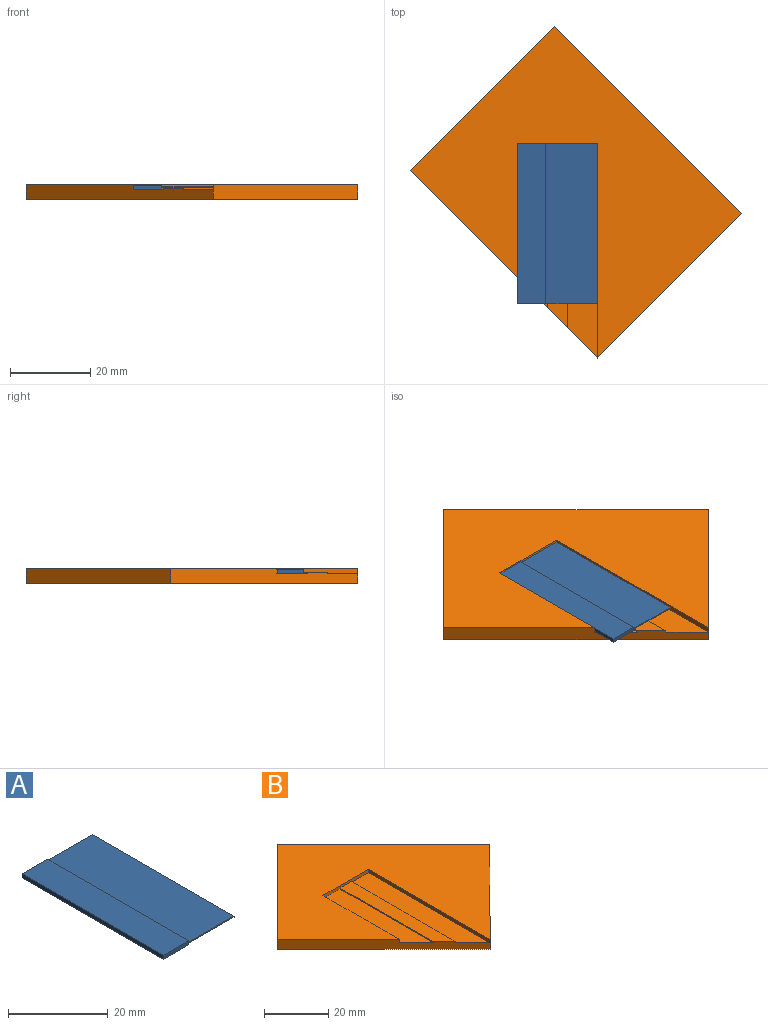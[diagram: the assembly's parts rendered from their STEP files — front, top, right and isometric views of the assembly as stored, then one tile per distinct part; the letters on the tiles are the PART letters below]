
ASSEMBLY  parts=2 mates=1
PART A: 10 faces, bbox 20x40x1 mm
  f0: plane 40x0.38mm, normal (1,0,0), area 15mm2, adj f2,f4,f6,f9
  f1: plane 40x1mm, normal (-1,0,0), area 40mm2, adj f2,f4,f5,f6
  f2: plane 20x1mm, normal (0,-1,0), area 10.4mm2, adj f0,f1,f3,f5,f6,f7,f8,f9
  f3: plane 40x0.38mm, normal (1,0,0), area 15mm2, adj f2,f4,f5,f8
  f4: plane 20x1mm, normal (0,1,0), area 10.4mm2, adj f0,f1,f3,f5,f6,f7,f8,f9
  f5: plane 40x7.2mm, normal (0,0,1), area 288mm2, adj f1,f2,f3,f4
  f6: plane 40x7.2mm, normal (0,0,-1), area 288mm2, adj f0,f1,f2,f4
  f7: plane 40x0.25mm, normal (1,0,0), area 10mm2, adj f2,f4,f8,f9
  f8: plane 40x12.8mm, normal (0,0,1), area 512mm2, adj f2,f3,f4,f7
  f9: plane 40x12.8mm, normal (0,0,-1), area 512mm2, adj f0,f2,f4,f7
PART B: 14 faces, bbox 82.7x82.7x3.7 mm
  f0: plane 41.06x7.5mm, normal (0,0,1), area 279.8mm2, adj f4,f9,f10,f11
  f1: plane 53.56x7.5mm, normal (0,0,1), area 373.5mm2, adj f4,f8,f9,f12
  f2: plane 82.73x82.73mm, normal (0,0,1), area 2494.9mm2, adj f3,f4,f5,f6,f8,f9,f10
  f3: plane 36.06x36.06mm, normal (-0.71,0.71,0), area 188.7mm2, adj f2,f4,f6,f7
  f4: plane 46.67x46.67mm, normal (-0.71,-0.71,0), area 210.3mm2, adj f0,f1,f2,f3,f5,f7,f10,f11
  f5: plane 36.06x36.06mm, normal (0.71,-0.71,0), area 188.7mm2, adj f2,f4,f6,f7,f8
  f6: plane 46.67x46.67mm, normal (0.71,0.71,0), area 244.2mm2, adj f2,f3,f5,f7
  f7: plane 82.73x82.73mm, normal (0,0,-1), area 3366mm2, adj f3,f4,f5,f6
  f8: plane 53.56x1.3mm, normal (-1,0,0), area 69.6mm2, adj f1,f2,f5,f9
  f9: plane 20x1.3mm, normal (0,-1,0), area 24mm2, adj f0,f1,f2,f8,f10,f11,f12,f13
  f10: plane 33.56x1.3mm, normal (1,0,0), area 43.6mm2, adj f0,f2,f4,f9
  f11: plane 41.06x0.4mm, normal (-1,0,0), area 16.4mm2, adj f0,f4,f9,f13
  f12: plane 46.06x0.4mm, normal (1,0,0), area 18.4mm2, adj f1,f4,f9,f13
  f13: plane 46.06x5mm, normal (0,0,1), area 217.8mm2, adj f4,f9,f11,f12
PLACE A t=(8.66,60.95,-18.44)mm
PLACE B t=(8.66,0,-19.09)mm fixed
MATE planar B.f10 <-> A.f1  axis (1,0,0) through (-11.34,21.22,-18.44)mm
